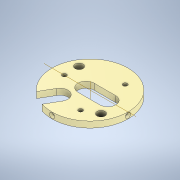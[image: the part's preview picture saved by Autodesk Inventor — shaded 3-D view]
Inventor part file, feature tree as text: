
AUTODESK INVENTOR PART (.ipt)
format: ipt  version: 2021 (Build 250183000, 183)  size: 191,488 bytes
history: native  units: in
note: dims shown in document units (in); Inventor stores cm internally (conversion verified against a paired STEP export)
features: plane x2, other x2, extrude x1, hole x1, pattern_circular x1, sketch x1
ambient origin geometry x8: Origin, YZ Plane, XZ Plane, XY Plane, X Axis, Y Axis, Z Axis, Center Point
bodies: Solid1 (feature_tree)
feature tree (8):
  extrude  "Extrusion1"  TaperAngle=60.0deg  [1 undecoded]
  plane  "Work Plane2"
  hole  "Hole1"  [1 undecoded]
  other  "Work Axis2"
  pattern_circular  "Circular Pattern1"  Angle=30.0deg  [1 undecoded]
  other  "Work Axis1"
  plane  "Work Plane1"
  sketch  "Sketch2"  dims[d0=4.75in d1=60.0deg d2=120.0deg d3=30.0deg d10=3.75in d12=2.76in d14=3.2165in d16=1.1811in d18=360.0deg d20=0.7874in d22=360.0deg d25=0.0in d26=0.25in d27=1.358in d28=1.0in d29=1.0in d31=0.0in d32=0.19in d33=0.13in d34=0.328in d35=0.332in d36=0.25in d37=0.5635in d38=0.484in d39=0.8108in d40=1.5748in d41=360.0deg d42=0.0625in d43=0.75in d44=0.375in]
note: 3 required parameter values undecoded (feature->parameter linkage not recoverable at this tier; creation-order binding heuristic only, values carry confidence <= 0.55)
